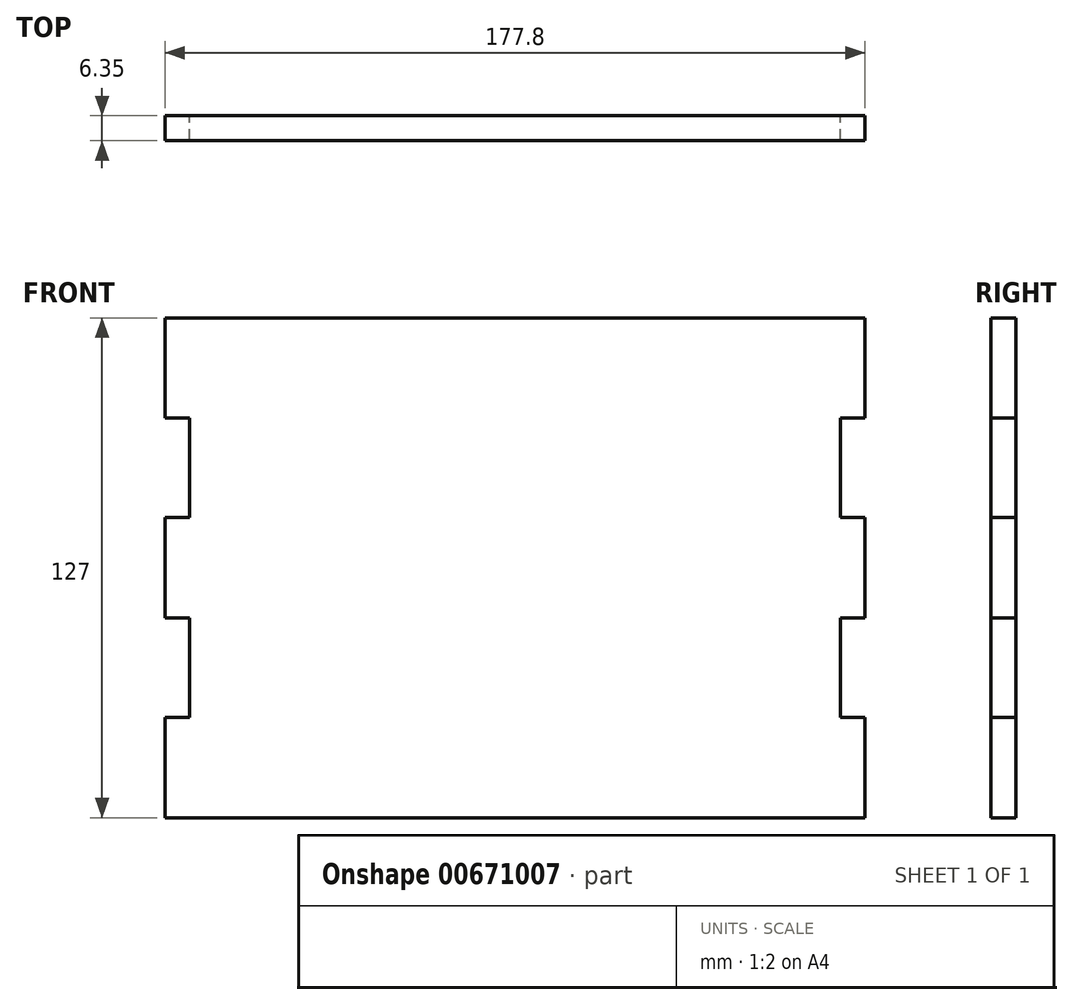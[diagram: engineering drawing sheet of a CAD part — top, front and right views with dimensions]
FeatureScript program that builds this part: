
annotation { "Feature Type Name" : "Feature", "Feature Type Description" : "" }
export const myFeature = defineFeature(function(context is Context, id is Id, definition is map)
    precondition{}
    {
        {
            var Q0;
            Q0=qCreatedBy(makeId("Front.planeOp"),FACE);
            var sketch = newSketch(context, id + "F0", { "sketchPlane" : qUnion([Q0])});
            skLineSegment(sketch, "E0.bottom", {"start": v(0, 0) * mm, "end": v(177.8, 0) * mm});
            skLineSegment(sketch, "E0.top", {"start": v(0, 127) * mm, "end": v(177.8, 127) * mm});
            skLineSegment(sketch, "E0.left", {"start": v(0, 0) * mm, "end": v(0, 127) * mm});
            skLineSegment(sketch, "E0.right", {"start": v(177.8, 0) * mm, "end": v(177.8, 127) * mm});
            skLineSegment(sketch, "E1.bottom", {"start": v(25.31, 0) * mm, "end": v(50.89, 0) * mm});
            skLineSegment(sketch, "E1.top", {"start": v(25.31, -6.44) * mm, "end": v(50.89, -6.44) * mm});
            skLineSegment(sketch, "E1.left", {"start": v(25.31, 0) * mm, "end": v(25.31, -6.44) * mm});
            skLineSegment(sketch, "E1.right", {"start": v(50.89, 0) * mm, "end": v(50.89, -6.44) * mm});
            skLineSegment(sketch, "E2.bottom", {"start": v(76.11, 0) * mm, "end": v(101.69, 0) * mm});
            skLineSegment(sketch, "E2.top", {"start": v(76.11, -6.44) * mm, "end": v(101.69, -6.44) * mm});
            skLineSegment(sketch, "E2.left", {"start": v(76.11, 0) * mm, "end": v(76.11, -6.44) * mm});
            skLineSegment(sketch, "E2.right", {"start": v(101.69, 0) * mm, "end": v(101.69, -6.44) * mm});
            skLineSegment(sketch, "E3.bottom", {"start": v(126.91, 0) * mm, "end": v(152.49, 0) * mm});
            skLineSegment(sketch, "E3.top", {"start": v(126.91, -6.44) * mm, "end": v(152.49, -6.44) * mm});
            skLineSegment(sketch, "E3.left", {"start": v(126.91, 0) * mm, "end": v(126.91, -6.44) * mm});
            skLineSegment(sketch, "E3.right", {"start": v(152.49, 0) * mm, "end": v(152.49, -6.44) * mm});
            skPoint(sketch, "E4", {"position": v(38.1, 0) * mm});
            skPoint(sketch, "E5", {"position": v(88.9, 0) * mm});
            skPoint(sketch, "E6", {"position": v(139.7, 0) * mm});
            skLineSegment(sketch, "E7.bottom", {"start": v(0, 101.51) * mm, "end": v(6.26, 101.51) * mm});
            skLineSegment(sketch, "E7.top", {"start": v(0, 76.29) * mm, "end": v(6.26, 76.29) * mm});
            skLineSegment(sketch, "E7.left", {"start": v(0, 101.51) * mm, "end": v(0, 76.29) * mm});
            skLineSegment(sketch, "E7.right", {"start": v(6.26, 101.51) * mm, "end": v(6.26, 76.29) * mm});
            skLineSegment(sketch, "E8.bottom", {"start": v(177.8, 101.51) * mm, "end": v(171.54, 101.51) * mm});
            skLineSegment(sketch, "E8.top", {"start": v(177.8, 76.29) * mm, "end": v(171.54, 76.29) * mm});
            skLineSegment(sketch, "E8.left", {"start": v(177.8, 101.51) * mm, "end": v(177.8, 76.29) * mm});
            skLineSegment(sketch, "E8.right", {"start": v(171.54, 101.51) * mm, "end": v(171.54, 76.29) * mm});
            skPoint(sketch, "E9", {"position": v(0, 88.9) * mm});
            skPoint(sketch, "E10", {"position": v(177.8, 88.9) * mm});
            skLineSegment(sketch, "E11", {"start": v(177.8, 50.71) * mm, "end": v(171.54, 50.71) * mm});
            skLineSegment(sketch, "E12", {"start": v(171.54, 50.71) * mm, "end": v(171.54, 25.49) * mm});
            skLineSegment(sketch, "E13", {"start": v(171.54, 25.49) * mm, "end": v(177.8, 25.49) * mm});
            skPoint(sketch, "E14", {"position": v(171.54, 38.1) * mm});
            skLineSegment(sketch, "E15", {"start": v(88.9, 127) * mm, "end": v(88.9, 0) * mm, "construction": true});
            skLineSegment(sketch, "E16.MirrorCS", {"start": v(0, 50.71) * mm, "end": v(6.26, 50.71) * mm});
            skPoint(sketch, "E17.MirrorP", {"position": v(6.26, 38.1) * mm});
            skLineSegment(sketch, "E18.MirrorCS", {"start": v(6.26, 25.49) * mm, "end": v(0, 25.49) * mm});
            skLineSegment(sketch, "E19.MirrorCS", {"start": v(6.26, 50.71) * mm, "end": v(6.26, 25.49) * mm});
            skSolve(sketch);
        }
        {
            var Q0;
            {var subQ2=sQuery(id+"F0.wireOp",EDGE,"E0.top");Q0=makeQuery(id+"F0.imprint","IMPRINT",FACE,{"disambiguationData":[TD([[makeQuery(id+"F0.imprint","IMPRINT",EDGE,{"derivedFrom":subQ2}),-1.0]])]});}
            var Q1;
            Q1=makeQuery(id+"F0.imprint","IMPRINT",FACE,{"disambiguationData":[TD([[makeQuery(id+"F0.imprint","IMPRINT",EDGE,{"derivedFrom":sQuery(id+"F0.wireOp",EDGE,"E1.bottom")}),-1.0]])]});
            var Q2;
            Q2=makeQuery(id+"F0.imprint","IMPRINT",FACE,{"disambiguationData":[TD([[makeQuery(id+"F0.imprint","IMPRINT",EDGE,{"derivedFrom":sQuery(id+"F0.wireOp",EDGE,"E2.bottom")}),-1.0]])]});
            var Q3;
            Q3=makeQuery(id+"F0.imprint","IMPRINT",FACE,{"disambiguationData":[TD([[makeQuery(id+"F0.imprint","IMPRINT",EDGE,{"derivedFrom":sQuery(id+"F0.wireOp",EDGE,"E3.bottom")}),-1.0]])]});
            extrude(context, id + "F1", {"entities" : qUnion([Q0, Q1, Q2, Q3]), "depth" : 6.35 * mm, "offsetDistance" : 25.4 * mm});
        }
    });
